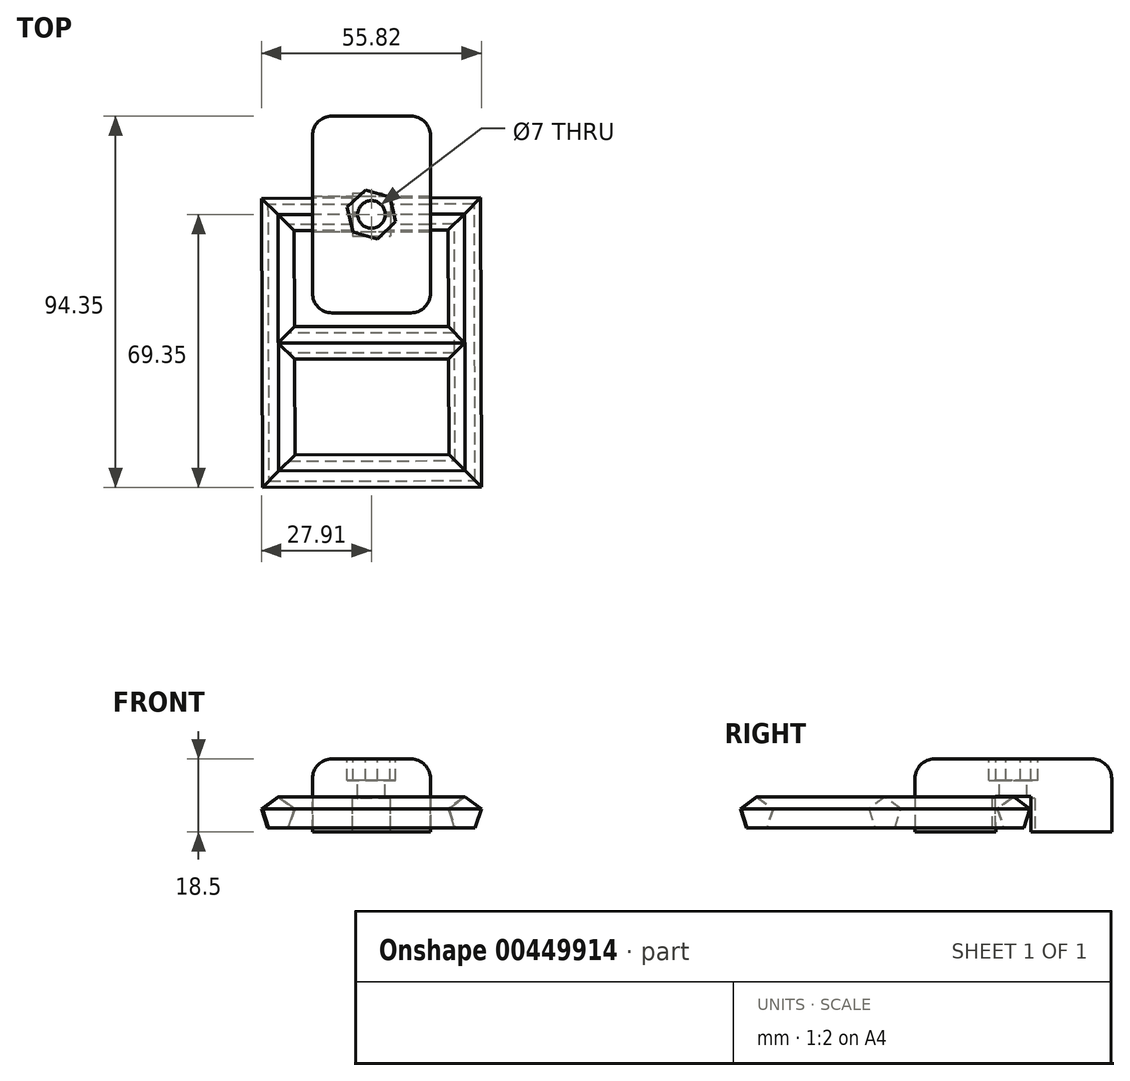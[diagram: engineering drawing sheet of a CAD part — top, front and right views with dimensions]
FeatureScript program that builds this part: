
annotation { "Feature Type Name" : "Feature", "Feature Type Description" : "" }
export const myFeature = defineFeature(function(context is Context, id is Id, definition is map)
    precondition{}
    {
        {
            var Q0;
            Q0=qCreatedBy(makeId("Top.planeOp"),FACE);
            var sketch = newSketch(context, id + "F0", { "sketchPlane" : qUnion([Q0])});
            skLineSegment(sketch, "E0.bottom", {"start": v(15, 25) * mm, "end": v(-15, 25) * mm});
            skLineSegment(sketch, "E0.top", {"start": v(15, -25) * mm, "end": v(-15, -25) * mm});
            skLineSegment(sketch, "E0.left", {"start": v(15, 25) * mm, "end": v(15, -25) * mm});
            skLineSegment(sketch, "E0.right", {"start": v(-15, 25) * mm, "end": v(-15, -25) * mm});
            skPoint(sketch, "E0.middle", {"position": v(0, 0) * mm});
            skSolve(sketch);
        }
        {
            var Q0;
            Q0 = qSketchRegion(id + "F0", true);
            var Q1;
            Q1=makeQuery(id+"F0.imprint","IMPRINT",FACE,{"disambiguationData":[TD([[makeQuery(id+"F0.imprint","IMPRINT",EDGE,{"derivedFrom":sQuery(id+"F0.wireOp",EDGE,"E0.bottom")}),1.0]])]});
            extrude(context, id + "F1", {"entities" : qUnion([Q0, Q1]), "depth" : 18.5 * mm});
        }
        {
            var Q0;
            Q0=makeQuery(id+"F1.opExtrude","SWEPT_EDGE",EDGE,{"disambiguationData":[OSD([sQuery(id+"F0.wireOp",EDGE,"E0.top"),sQuery(id+"F0.wireOp",EDGE,"E0.left")])]});
            var Q1;
            Q1=makeQuery(id+"F1.opExtrude","SWEPT_EDGE",EDGE,{"disambiguationData":[OSD([sQuery(id+"F0.wireOp",EDGE,"E0.top"),sQuery(id+"F0.wireOp",EDGE,"E0.right")])]});
            var Q2;
            Q2=makeQuery(id+"F1.opExtrude","SWEPT_EDGE",EDGE,{"disambiguationData":[OSD([sQuery(id+"F0.wireOp",EDGE,"E0.bottom"),sQuery(id+"F0.wireOp",EDGE,"E0.right")])]});
            var Q3;
            Q3=makeQuery(id+"F1.opExtrude","SWEPT_EDGE",EDGE,{"disambiguationData":[OSD([sQuery(id+"F0.wireOp",EDGE,"E0.bottom"),sQuery(id+"F0.wireOp",EDGE,"E0.left")])]});
            fillet(context, id + "F2", {"entities" : qUnion([Q0, Q1, Q2, Q3]), "radius" : 5 * mm, "tangentPropagation" : true, "allowEdgeOverflow" : false});
        }
        {
            var Q0;
            {var subQ0=sQuery(id+"F0.wireOp",EDGE,"E0.left");var subQ1=sQuery(id+"F0.wireOp",EDGE,"E0.top");Q0=makeQuery(id+"F2.opFillet","BLEND_EDGE",EDGE,{"blendedFrom":[makeQuery(id+"F1.opExtrude","SWEPT_EDGE",EDGE,{"disambiguationData":[OSD([subQ1,subQ0])]}),makeQuery(id+"F1.opExtrude","CAP_FACE",FACE,{"disambiguationData":[OSD([sQuery(id+"F0.wireOp",EDGE,"E0.bottom"),subQ1,subQ0,sQuery(id+"F0.wireOp",EDGE,"E0.right")])],"isStart":false})],"blendedInto":[makeQuery(id+"F1.opExtrude","CAP_FACE",FACE,{"disambiguationData":[OSD([sQuery(id+"F0.wireOp",EDGE,"E0.bottom"),subQ1,subQ0,sQuery(id+"F0.wireOp",EDGE,"E0.right")])],"isStart":false})]});}
            fillet(context, id + "F3", {"entities" : qUnion([Q0]), "radius" : 5 * mm, "tangentPropagation" : true, "allowEdgeOverflow" : false});
        }
        {
            var Q0;
            Q0=makeQuery(id+"F1.opExtrude","CAP_FACE",FACE,{"disambiguationData":[OSD([sQuery(id+"F0.wireOp",EDGE,"E0.bottom"),sQuery(id+"F0.wireOp",EDGE,"E0.top"),sQuery(id+"F0.wireOp",EDGE,"E0.left"),sQuery(id+"F0.wireOp",EDGE,"E0.right")])],"isStart":false});
            var sketch = newSketch(context, id + "F4", { "sketchPlane" : qUnion([Q0])});
            skCircle(sketch, "E1.cCircle", {"center": v(0, 0) * mm, "radius": 5.56 * mm, "construction": true});
            skLineSegment(sketch, "E1.0", {"start": v(-1.5, 6.25) * mm, "end": v(4.66, 4.42) * mm});
            skLineSegment(sketch, "E1.1", {"start": v(4.66, 4.42) * mm, "end": v(6.16, -1.83) * mm});
            skLineSegment(sketch, "E1.2", {"start": v(6.16, -1.83) * mm, "end": v(1.5, -6.25) * mm});
            skLineSegment(sketch, "E1.3", {"start": v(1.5, -6.25) * mm, "end": v(-4.66, -4.42) * mm});
            skLineSegment(sketch, "E1.4", {"start": v(-4.66, -4.42) * mm, "end": v(-6.16, 1.83) * mm});
            skLineSegment(sketch, "E1.5", {"start": v(-6.16, 1.83) * mm, "end": v(-1.5, 6.25) * mm});
            skPoint(sketch, "E1.0.midPoint", {"position": v(1.58, 5.33) * mm});
            skSolve(sketch);
        }
        {
            var Q0;
            Q0 = qSketchRegion(id + "F4", true);
            extrude(context, id + "F5", {"entities" : qUnion([Q0]), "operationType" : NewBodyOperationType.REMOVE, "oppositeDirection" : true, "depth" : 5.5 * mm});
        }
        {
            var Q0;
            Q0=makeQuery(id+"F1.opExtrude","SWEPT_FACE",FACE,{"disambiguationData":[OSD([sQuery(id+"F0.wireOp",EDGE,"E0.left")])]});
            var sketch = newSketch(context, id + "F6", { "sketchPlane" : qUnion([Q0])});
            skLineSegment(sketch, "E2", {"start": v(-25, 7.75) * mm, "end": v(25, 7.75) * mm, "construction": true});
            skLineSegment(sketch, "E3", {"start": v(0, 15.5) * mm, "end": v(0, 0) * mm, "construction": true});
            skSolve(sketch);
        }
        {
            var Q0;
            Q0=qCreatedBy(makeId("Top.planeOp"),FACE);
            cPlane(context, id + "F7", {"entities" : qUnion([Q0]), "cplaneType" : CPlaneType.OFFSET, "offset" : 4.5 * mm, "width" : 150 * mm, "height" : 150 * mm});
        }
        {
            var Q0;
            Q0=qCreatedBy(id+"F7.planeOp",FACE);
            var sketch = newSketch(context, id + "F8", { "sketchPlane" : qUnion([Q0])});
            skCircle(sketch, "E4.cCircle", {"center": v(0, -32.55) * mm, "radius": 40.33 * mm, "construction": true});
            skLineSegment(sketch, "E4.0", {"start": v(-23.81, 0) * mm, "end": v(23.6, 0.15) * mm});
            skLineSegment(sketch, "E4.3", {"start": v(23.81, -65.1) * mm, "end": v(-23.6, -65.25) * mm});
            skLineSegment(sketch, "E5", {"start": v(-23.81, 0) * mm, "end": v(-23.6, -65.25) * mm});
            skLineSegment(sketch, "E6", {"start": v(23.6, 0.15) * mm, "end": v(23.81, -65.1) * mm});
            skLineSegment(sketch, "E7", {"start": v(-23.7, -32.63) * mm, "end": v(23.7, -32.63) * mm});
            skSolve(sketch);
        }
        {
            var Q0;
            Q0=makeQuery(id+"F1.opExtrude","SWEPT_FACE",FACE,{"disambiguationData":[OSD([sQuery(id+"F0.wireOp",EDGE,"E0.right")])]});
            var sketch = newSketch(context, id + "F9", { "sketchPlane" : qUnion([Q0])});
            skLineSegment(sketch, "E8.0", {"start": v(0, 4.5) * mm, "end": v(-0.15, 4.5) * mm});
            skCircle(sketch, "E9.cCircle", {"center": v(0, 4.5) * mm, "radius": 3.5 * mm, "construction": true});
            skLineSegment(sketch, "E9.0", {"start": v(2.54, 1) * mm, "end": v(-2.54, 1) * mm});
            skLineSegment(sketch, "E9.1", {"start": v(-2.54, 1) * mm, "end": v(-4.11, 5.84) * mm});
            skLineSegment(sketch, "E9.2", {"start": v(-4.11, 5.84) * mm, "end": v(0, 8.83) * mm});
            skLineSegment(sketch, "E9.3", {"start": v(0, 8.83) * mm, "end": v(4.11, 5.84) * mm});
            skLineSegment(sketch, "E9.4", {"start": v(4.11, 5.84) * mm, "end": v(2.54, 1) * mm});
            skPoint(sketch, "E9.0.midPoint", {"position": v(0, 1) * mm});
            skSolve(sketch);
        }
        {
            var Q0;
            Q0=makeQuery(id+"F9.imprint","IMPRINT",FACE,{"disambiguationData":[TD([[makeQuery(id+"F9.imprint","IMPRINT",EDGE,{"derivedFrom":sQuery(id+"F9.wireOp",EDGE,"E9.0")}),-1.0]])]});
            var Q1;
            Q1=sQuery(id+"F8.wireOp",EDGE,"E4.0");
            var Q2;
            Q2=sQuery(id+"F8.wireOp",EDGE,"E5");
            var Q3;
            Q3=sQuery(id+"F8.wireOp",EDGE,"E4.3");
            var Q4;
            Q4=sQuery(id+"F8.wireOp",EDGE,"E6");
            sweep(context, id + "F10", {"operationType" : NewBodyOperationType.ADD, "profiles" : qUnion([Q0]), "path" : qUnion([Q1, Q2, Q3, Q4])});
        }
        {
            var Q0;
            Q0=qCreatedBy(makeId("Right.planeOp"),FACE);
            var sketch = newSketch(context, id + "F11", { "sketchPlane" : qUnion([Q0])});
            skLineSegment(sketch, "E10.0", {"start": v(-32.63, 4.5) * mm, "end": v(-32.77, 4.5) * mm});
            skCircle(sketch, "E11.cCircle", {"center": v(-32.63, 4.5) * mm, "radius": 3.5 * mm, "construction": true});
            skLineSegment(sketch, "E11.0", {"start": v(-30.08, 1) * mm, "end": v(-35.17, 1) * mm});
            skLineSegment(sketch, "E11.1", {"start": v(-35.17, 1) * mm, "end": v(-36.74, 5.84) * mm});
            skLineSegment(sketch, "E11.2", {"start": v(-36.74, 5.84) * mm, "end": v(-32.63, 8.83) * mm});
            skLineSegment(sketch, "E11.3", {"start": v(-32.63, 8.83) * mm, "end": v(-28.51, 5.84) * mm});
            skLineSegment(sketch, "E11.4", {"start": v(-28.51, 5.84) * mm, "end": v(-30.08, 1) * mm});
            skPoint(sketch, "E11.0.midPoint", {"position": v(-32.63, 1) * mm});
            skSolve(sketch);
        }
        {
            var Q0;
            Q0=makeQuery(id+"F11.imprint","IMPRINT",FACE,{"disambiguationData":[TD([[makeQuery(id+"F11.imprint","IMPRINT",EDGE,{"derivedFrom":sQuery(id+"F11.wireOp",EDGE,"E11.0")}),-1.0]])]});
            extrude(context, id + "F12", {"entities" : qUnion([Q0]), "endBound" : BoundingType.UP_TO_NEXT, "depth" : 40 * mm, "hasSecondDirection" : true, "secondDirectionBound" : SecondDirectionBoundingType.UP_TO_NEXT, "secondDirectionOppositeDirection" : true, "secondDirectionDepth" : 25 * mm});
        }
        {
            var Q0;
            Q0=makeQuery(id+"F1.opExtrude","CAP_FACE",FACE,{"disambiguationData":[OSD([sQuery(id+"F0.wireOp",EDGE,"E0.bottom"),sQuery(id+"F0.wireOp",EDGE,"E0.top"),sQuery(id+"F0.wireOp",EDGE,"E0.left"),sQuery(id+"F0.wireOp",EDGE,"E0.right")])],"isStart":false});
            var sketch = newSketch(context, id + "F13", { "sketchPlane" : qUnion([Q0])});
            skCircle(sketch, "E12", {"center": v(0, 0) * mm, "radius": 3.5 * mm});
            skSolve(sketch);
        }
        {
            var Q0;
            Q0=makeQuery(id+"F13.imprint","IMPRINT",FACE,{"disambiguationData":[TD([[makeQuery(id+"F13.imprint","IMPRINT",EDGE,{"derivedFrom":sQuery(id+"F13.wireOp",EDGE,"E12")}),1.0]])]});
            extrude(context, id + "F14", {"entities" : qUnion([Q0]), "operationType" : NewBodyOperationType.REMOVE, "oppositeDirection" : true, "depth" : 25 * mm});
        }
        {
            var Q0;
            Q0=makeQuery(id+"F9.imprint","IMPRINT",FACE,{"disambiguationData":[TD([[makeQuery(id+"F9.imprint","IMPRINT",EDGE,{"derivedFrom":sQuery(id+"F9.wireOp",EDGE,"E9.0")}),1.0]])]});
            var sketch = newSketch(context, id + "F15", { "sketchPlane" : qUnion([Q0])});
            skCircle(sketch, "E13.0", {"center": v(0, 4.5) * mm, "radius": 3.5 * mm});
            skLineSegment(sketch, "E14", {"start": v(-3.48, 0) * mm, "end": v(-3.54, 15.62) * mm, "construction": true});
            skLineSegment(sketch, "E15", {"start": v(3.45, 0) * mm, "end": v(3.63, 15.58) * mm, "construction": true});
            skLineSegment(sketch, "E16.0", {"start": v(-4.48, 0) * mm, "end": v(-4.52, 8.96) * mm});
            skLineSegment(sketch, "E17.MirrorCS", {"start": v(4.48, 0) * mm, "end": v(4.52, 9.04) * mm});
            skLineSegment(sketch, "E18", {"start": v(-24.97, 7.8) * mm, "end": v(25.06, 8.2) * mm, "construction": true});
            skPoint(sketch, "E18.startSnap0", {"position": v(-4.51, 7.8) * mm});
            skLineSegment(sketch, "E19.0", {"start": v(-4.52, 8.96) * mm, "end": v(4.52, 9.04) * mm});
            skPoint(sketch, "E20.orphan", {"position": v(-4.54, 15.61) * mm});
            skPoint(sketch, "E21.orphan", {"position": v(4.54, 15.61) * mm});
            skLineSegment(sketch, "E22", {"start": v(-4.48, 0) * mm, "end": v(4.48, 0) * mm});
            skSolve(sketch);
        }
        {
            var Q0;
            {var subQ9=sQuery(id+"F15.wireOp",EDGE,"E19.0");Q0=makeQuery(id+"F15.imprint","IMPRINT",FACE,{"disambiguationData":[TD([[makeQuery(id+"F15.imprint","IMPRINT",EDGE,{"derivedFrom":subQ9}),-1.0]])]});}
            extrude(context, id + "F16", {"entities" : qUnion([Q0]), "operationType" : NewBodyOperationType.REMOVE, "oppositeDirection" : true, "depth" : 30 * mm});
        }
        {
            var Q0;
            Q0=makeQuery(id+"F0.imprint","IMPRINT",FACE,{"disambiguationData":[TD([[makeQuery(id+"F0.imprint","IMPRINT",EDGE,{"derivedFrom":sQuery(id+"F0.wireOp",EDGE,"E0.bottom")}),1.0]])]});
            var sketch = newSketch(context, id + "F17", { "sketchPlane" : qUnion([Q0])});
            skLineSegment(sketch, "E23.bottom", {"start": v(-4.78, 5.47) * mm, "end": v(4.78, 5.47) * mm});
            skLineSegment(sketch, "E23.top", {"start": v(-4.78, -5.47) * mm, "end": v(4.78, -5.47) * mm});
            skLineSegment(sketch, "E23.left", {"start": v(-4.78, 5.47) * mm, "end": v(-4.78, -5.47) * mm});
            skLineSegment(sketch, "E23.right", {"start": v(4.78, 5.47) * mm, "end": v(4.78, -5.47) * mm});
            skPoint(sketch, "E23.middle", {"position": v(0, 0) * mm});
            skSolve(sketch);
        }
        {
            var Q0;
            Q0=makeQuery(id+"F17.imprint","IMPRINT",FACE,{"disambiguationData":[TD([[makeQuery(id+"F17.imprint","IMPRINT",EDGE,{"derivedFrom":sQuery(id+"F17.wireOp",EDGE,"E23.bottom")}),-1.0]])]});
            extrude(context, id + "F18", {"entities" : qUnion([Q0]), "operationType" : NewBodyOperationType.REMOVE, "depth" : 8.5 * mm});
        }
    });
